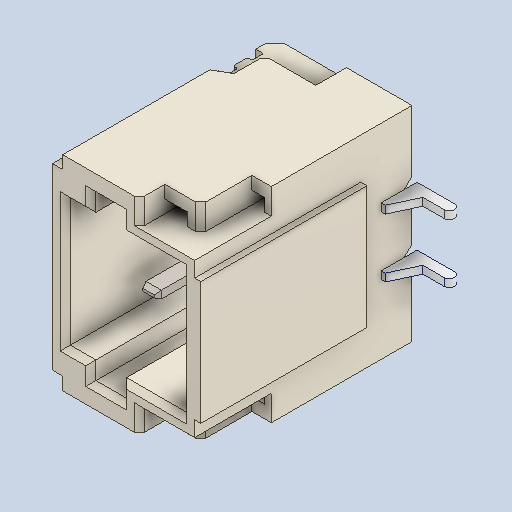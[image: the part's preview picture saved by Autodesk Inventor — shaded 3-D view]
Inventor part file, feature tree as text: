
AUTODESK INVENTOR PART (.ipt)
format: ipt  version: 2024.3 (Build 283343000, 343)  size: 245,248 bytes
history: native  units: in
note: dims shown in document units (in); Inventor stores cm internally (conversion verified against a paired STEP export)
features: other x2, chamfer x1, mirror x1
ambient origin geometry x8: Origin, YZ Plane, XZ Plane, XY Plane, X Axis, Y Axis, Z Axis, Center Point
bodies: Solid1 (feature_tree), Solid2 (feature_tree), Solid3 (feature_tree), Solid4 (feature_tree), Solid5 (feature_tree), Solid6 (feature_tree), Solid7 (feature_tree)
feature tree (4):
  chamfer  "Chamfer3"  [1 undecoded]
  mirror  "Mirror2"
  other  "Szyk liniowy1"
  other  "Szyk liniowy2"
note: 1 required parameter value undecoded (feature->parameter linkage not recoverable at this tier; creation-order binding heuristic only, values carry confidence <= 0.55)
